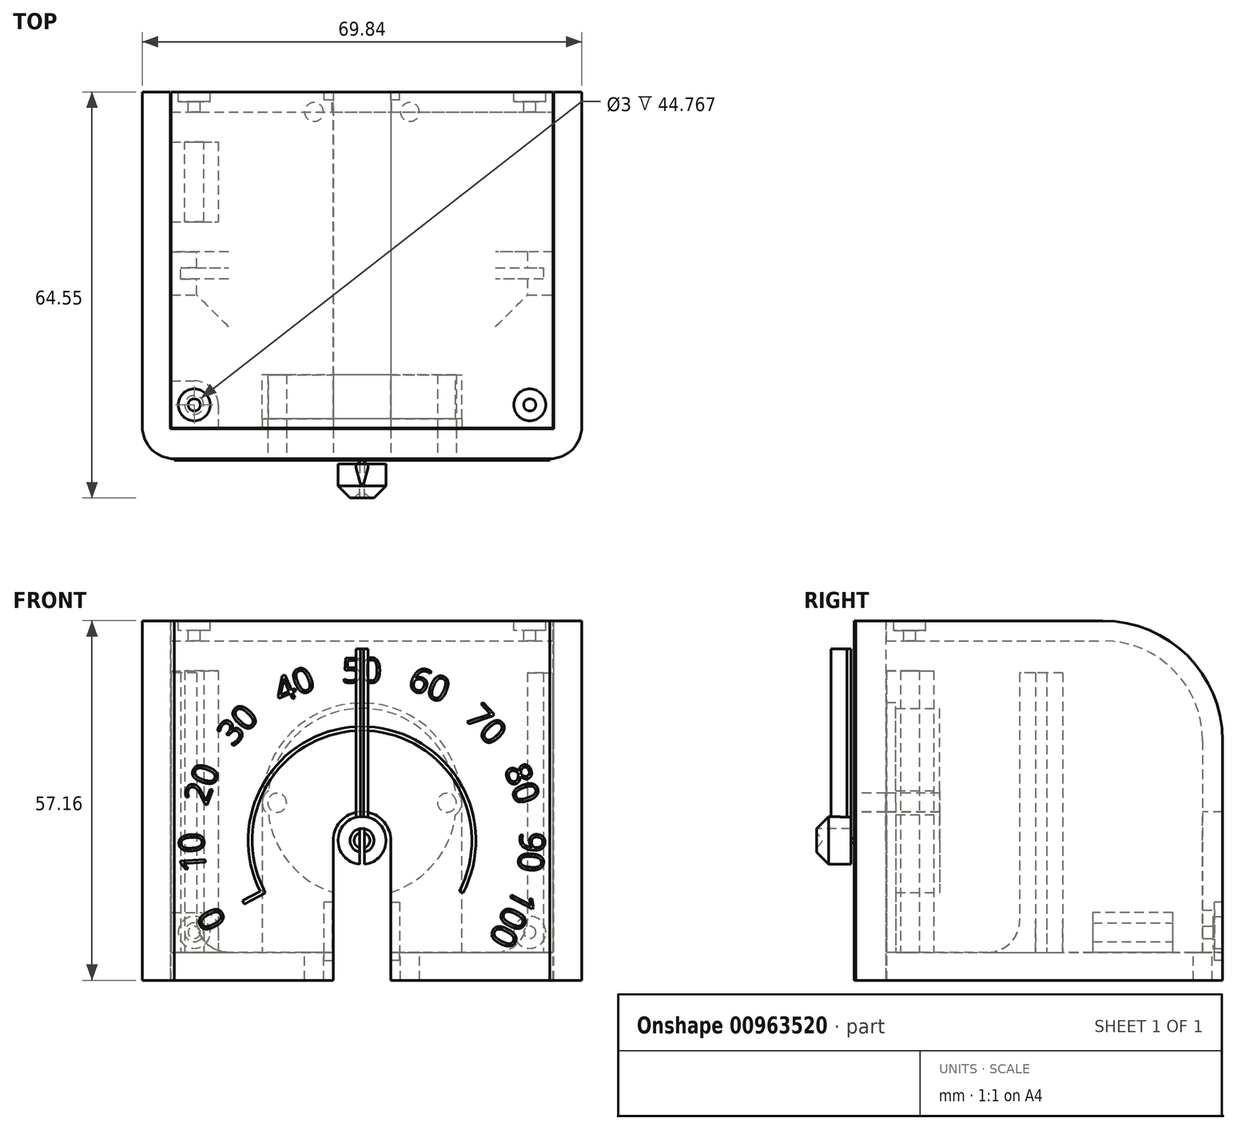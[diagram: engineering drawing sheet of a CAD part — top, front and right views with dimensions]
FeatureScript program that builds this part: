
annotation { "Feature Type Name" : "Feature", "Feature Type Description" : "" }
export const myFeature = defineFeature(function(context is Context, id is Id, definition is map)
    precondition{}
    {
        {
            var Q0;
            Q0=qCreatedBy(makeId("Front.planeOp"),FACE);
            var sketch = newSketch(context, id + "F0", { "sketchPlane" : qUnion([Q0])});
            skArc(sketch, "E0", {"start": v(-14.88, -1.9) * mm, "mid": v(0, -15) * mm, "end": v(14.88, -1.9) * mm});
            skArc(sketch, "E1", {"start": v(-14.88, 1.9) * mm, "mid": v(-15.85, 0) * mm, "end": v(-14.88, -1.9) * mm});
            skArc(sketch, "E2", {"start": v(14.88, -1.9) * mm, "mid": v(15.85, 0) * mm, "end": v(14.88, 1.9) * mm});
            skLineSegment(sketch, "E3", {"start": v(13.5, 0) * mm, "end": v(-13.5, 0) * mm, "construction": true});
            skArc(sketch, "E4.trimOffspring", {"start": v(14.88, 1.9) * mm, "mid": v(0, 15) * mm, "end": v(-14.88, 1.9) * mm});
            skCircle(sketch, "E5", {"center": v(-13.5, 0) * mm, "radius": 0.93 * mm});
            skCircle(sketch, "E6", {"center": v(13.5, 0) * mm, "radius": 0.93 * mm});
            skSolve(sketch);
        }
        {
            var Q0;
            Q0=qSketchRegion(id+"F0",true);
            extrude(context, id + "F1", {"entities" : qUnion([Q0]), "depth" : 7 * mm, "offsetDistance" : 25.4 * mm});
        }
        {
            var Q0;
            Q0=qCreatedBy(makeId("Right.planeOp"),FACE);
            var sketch = newSketch(context, id + "F2", { "sketchPlane" : qUnion([Q0])});
            skLineSegment(sketch, "E7.0", {"start": v(-7, -1.9) * mm, "end": v(-7, -15) * mm, "construction": true});
            skLineSegment(sketch, "E8", {"start": v(-7, -6) * mm, "end": v(-18, -6) * mm});
            skLineSegment(sketch, "E9", {"start": v(-18, -6) * mm, "end": v(-18, -5.5) * mm});
            skLineSegment(sketch, "E10", {"start": v(-18, -5.5) * mm, "end": v(-9.5, -5.5) * mm});
            skLineSegment(sketch, "E11", {"start": v(-9.5, -5.5) * mm, "end": v(-9.5, -5) * mm});
            skLineSegment(sketch, "E12", {"start": v(-9.5, -5) * mm, "end": v(-7, -5) * mm});
            skLineSegment(sketch, "E13", {"start": v(-7, -5) * mm, "end": v(-7, -6) * mm});
            skSolve(sketch);
        }
        {
            var Q0;
            Q0=qSketchRegion(id+"F2",true);
            var Q1;
            Q1=sQuery(id+"F2.wireOp",EDGE,"E8");
            revolve(context, id + "F3", {"operationType" : NewBodyOperationType.ADD, "surfaceOperationType" : NewSurfaceOperationType.NEW, "entities" : qUnion([Q0]), "axis" : qUnion([Q1]), "revolveType" : RevolveType.FULL});
        }
        {
            var Q0;
            Q0=makeQuery(id+"F3.opRevolve","SWEPT_EDGE",EDGE,{"disambiguationData":[OSD([sQuery(id+"F2.wireOp",EDGE,"E9"),sQuery(id+"F2.wireOp",EDGE,"E10")])]});
            chamfer(context, id + "F4", {"entities" : qUnion([Q0]), "chamferType" : ChamferType.OFFSET_ANGLE, "width" : 0.25 * mm, "oppositeDirection" : false, "angle" : 30 * degree, "tangentPropagation" : true});
        }
        {
            var Q0;
            Q0=makeQuery(id+"F1.opExtrude","CAP_FACE",FACE,{"disambiguationData":[OSD([sQuery(id+"F0.wireOp",EDGE,"E0"),sQuery(id+"F0.wireOp",EDGE,"E1"),sQuery(id+"F0.wireOp",EDGE,"E2"),sQuery(id+"F0.wireOp",EDGE,"E4.trimOffspring"),sQuery(id+"F0.wireOp",EDGE,"E5"),sQuery(id+"F0.wireOp",EDGE,"E6")])],"isStart":false});
            cPlane(context, id + "F5", {"entities" : qUnion([Q0]), "cplaneType" : CPlaneType.OFFSET, "offset" : 1.59 * mm, "width" : 152.4 * mm, "height" : 152.4 * mm});
        }
        {
            var Q0;
            Q0=qCreatedBy(id+"F5.planeOp",FACE);
            var sketch = newSketch(context, id + "F6", { "sketchPlane" : qUnion([Q0])});
            skLineSegment(sketch, "E14.bottom", {"start": v(-34.93, -25.05) * mm, "end": v(34.93, -25.05) * mm});
            skLineSegment(sketch, "E14.top", {"start": v(-34.93, 28.93) * mm, "end": v(34.93, 28.93) * mm});
            skLineSegment(sketch, "E14.left", {"start": v(-34.92, -25.05) * mm, "end": v(-34.92, 28.93) * mm});
            skLineSegment(sketch, "E14.right", {"start": v(34.92, -25.05) * mm, "end": v(34.92, 28.93) * mm});
            skPoint(sketch, "E14.middle", {"position": v(0, 0) * mm});
            skCircle(sketch, "E15.0", {"center": v(0, -6) * mm, "radius": 2.27 * mm});
            skLineSegment(sketch, "E16", {"start": v(0, 28.93) * mm, "end": v(0, 0) * mm, "construction": true});
            skLineSegment(sketch, "E17", {"start": v(0, -6) * mm, "end": v(22.45, 16.45) * mm, "construction": true});
            skLineSegment(sketch, "E18", {"start": v(0, -6) * mm, "end": v(-22.45, 16.45) * mm, "construction": true});
            skLineSegment(sketch, "E19", {"start": v(0, -6) * mm, "end": v(-27.5, -21.87) * mm, "construction": true});
            skLineSegment(sketch, "E20", {"start": v(0, -6) * mm, "end": v(27.5, -21.87) * mm, "construction": true});
            skLineSegment(sketch, "E21", {"start": v(0, -6) * mm, "end": v(0, 25.75) * mm, "construction": true});
            skCircle(sketch, "E22", {"center": v(0, -6) * mm, "radius": 31.75 * mm, "construction": true});
            skSolve(sketch);
        }
        {
            var Q0;
            Q0=qSketchRegion(id+"F6",true);
            extrude(context, id + "F7", {"entities" : qUnion([Q0]), "depth" : 4.76 * mm, "offsetDistance" : 25.4 * mm});
        }
        {
            var Q0;
            Q0=makeQuery(id+"F7.opExtrude","SWEPT_FACE",FACE,{"disambiguationData":[OSD([sQuery(id+"F6.wireOp",EDGE,"E14.bottom")])]});
            var sketch = newSketch(context, id + "F8", { "sketchPlane" : qUnion([Q0])});
            skLineSegment(sketch, "E23", {"start": v(-28.83, -15.24) * mm, "end": v(-26.29, -15.24) * mm});
            skLineSegment(sketch, "E24", {"start": v(-26.29, -15.24) * mm, "end": v(-26.29, -12.7) * mm});
            skLineSegment(sketch, "E25", {"start": v(-26.29, -12.7) * mm, "end": v(-31.75, -12.7) * mm});
            skLineSegment(sketch, "E26", {"start": v(-31.75, -12.7) * mm, "end": v(-31.75, -19.56) * mm});
            skLineSegment(sketch, "E27", {"start": v(-31.75, -19.56) * mm, "end": v(-26.29, -19.56) * mm});
            skLineSegment(sketch, "E28", {"start": v(-26.29, -19.56) * mm, "end": v(-26.29, -17.02) * mm});
            skLineSegment(sketch, "E29", {"start": v(-26.29, -17.02) * mm, "end": v(-28.83, -17.02) * mm});
            skLineSegment(sketch, "E30", {"start": v(-28.83, -17.02) * mm, "end": v(-28.83, -15.24) * mm});
            skLineSegment(sketch, "E31", {"start": v(-28.83, -16.13) * mm, "end": v(-31.75, -16.13) * mm, "construction": true});
            skSolve(sketch);
        }
        {
            var Q0;
            Q0 = qSketchRegion(id + "F8", true);
            extrude(context, id + "F9", {"entities" : qUnion([Q0]), "oppositeDirection" : true, "depth" : 45.72 * mm, "offsetDistance" : 25.4 * mm});
        }
        {
            var Q0;
            Q0=makeQuery(id+"F9.opExtrude","SWEPT_BODY",BODY,{"disambiguationData":[OSD([sQuery(id+"F8.wireOp",EDGE,"E23"),sQuery(id+"F8.wireOp",EDGE,"E24"),sQuery(id+"F8.wireOp",EDGE,"E25"),sQuery(id+"F8.wireOp",EDGE,"E26"),sQuery(id+"F8.wireOp",EDGE,"E27"),sQuery(id+"F8.wireOp",EDGE,"E28"),sQuery(id+"F8.wireOp",EDGE,"E29"),sQuery(id+"F8.wireOp",EDGE,"E30")])]});
            var Q1;
            Q1=qCreatedBy(makeId("Right.planeOp"),FACE);
            mirror(context, id + "F10", {"entities" : qUnion([Q0]), "mirrorPlane" : qUnion([Q1])});
        }
        {
            var Q0;
            Q0=makeQuery(id+"F7.opExtrude","CAP_FACE",FACE,{"disambiguationData":[OSD([sQuery(id+"F6.wireOp",EDGE,"E14.bottom"),sQuery(id+"F6.wireOp",EDGE,"E14.top"),sQuery(id+"F6.wireOp",EDGE,"E14.left"),sQuery(id+"F6.wireOp",EDGE,"E14.right"),sQuery(id+"F6.wireOp",EDGE,"E15.0")])],"isStart":true});
            var sketch = newSketch(context, id + "F11", { "sketchPlane" : qUnion([Q0])});
            skLineSegment(sketch, "E32", {"start": v(-34.92, 28.93) * mm, "end": v(-34.92, -28.23) * mm});
            skLineSegment(sketch, "E33", {"start": v(-34.92, -28.23) * mm, "end": v(34.93, -28.23) * mm});
            skLineSegment(sketch, "E34", {"start": v(34.92, -28.23) * mm, "end": v(34.92, 28.93) * mm});
            skLineSegment(sketch, "E35", {"start": v(34.93, 28.93) * mm, "end": v(31.75, 28.93) * mm});
            skLineSegment(sketch, "E36", {"start": v(31.75, 28.93) * mm, "end": v(31.75, -25.05) * mm, "construction": true});
            skLineSegment(sketch, "E37", {"start": v(31.75, -25.05) * mm, "end": v(-31.75, -25.05) * mm, "construction": true});
            skLineSegment(sketch, "E38", {"start": v(-31.75, -25.05) * mm, "end": v(-31.75, 28.93) * mm, "construction": true});
            skLineSegment(sketch, "E39", {"start": v(-31.75, 28.93) * mm, "end": v(-34.92, 28.93) * mm});
            skLineSegment(sketch, "E40.0", {"start": v(-30.48, -23.78) * mm, "end": v(-30.48, 28.93) * mm});
            skLineSegment(sketch, "E40.1", {"start": v(30.48, -23.78) * mm, "end": v(-30.48, -23.78) * mm});
            skLineSegment(sketch, "E40.2", {"start": v(30.48, 28.93) * mm, "end": v(30.48, -23.78) * mm});
            skLineSegment(sketch, "E41", {"start": v(-30.48, 28.93) * mm, "end": v(-31.75, 28.93) * mm});
            skLineSegment(sketch, "E42", {"start": v(30.48, 28.93) * mm, "end": v(31.75, 28.93) * mm});
            skSolve(sketch);
        }
        {
            var Q0;
            Q0 = qSketchRegion(id + "F11", true);
            var Q1;
            Q1=makeQuery(id+"F9.opExtrude","SWEPT_FACE",FACE,{"disambiguationData":[OSD([sQuery(id+"F8.wireOp",EDGE,"E27")])]});
            var Q2;
            Q2=makeQuery(id+"F7.opExtrude","CAP_FACE",FACE,{"disambiguationData":[OSD([sQuery(id+"F6.wireOp",EDGE,"E14.bottom"),sQuery(id+"F6.wireOp",EDGE,"E14.top"),sQuery(id+"F6.wireOp",EDGE,"E14.left"),sQuery(id+"F6.wireOp",EDGE,"E14.right"),sQuery(id+"F6.wireOp",EDGE,"E15.0")])],"isStart":false});
            extrude(context, id + "F12", {"entities" : qUnion([Q0]), "operationType" : NewBodyOperationType.ADD, "endBound" : BoundingType.UP_TO_SURFACE, "depth" : 25.4 * mm, "endBoundEntityFace" : qUnion([Q1]), "hasOffset" : true, "offsetDistance" : 25.4 * mm, "offsetOppositeDirection" : true, "hasSecondDirection" : true, "secondDirectionBound" : SecondDirectionBoundingType.UP_TO_SURFACE, "secondDirectionOppositeDirection" : true, "secondDirectionDepth" : 25.4 * mm, "secondDirectionBoundEntityFace" : qUnion([Q2])});
        }
        {
            var Q0;
            Q0=makeQuery(id+"F7.opExtrude","CAP_FACE",FACE,{"disambiguationData":[OSD([sQuery(id+"F6.wireOp",EDGE,"E14.bottom"),sQuery(id+"F6.wireOp",EDGE,"E14.top"),sQuery(id+"F6.wireOp",EDGE,"E14.left"),sQuery(id+"F6.wireOp",EDGE,"E14.right"),sQuery(id+"F6.wireOp",EDGE,"E15.0")])],"isStart":true});
            var sketch = newSketch(context, id + "F13", { "sketchPlane" : qUnion([Q0])});
            skArc(sketch, "E43", {"start": v(15.85, 0) * mm, "mid": v(0, 15.85) * mm, "end": v(-15.85, 0) * mm});
            skLineSegment(sketch, "E44", {"start": v(-15.85, 0) * mm, "end": v(-15.85, -23.78) * mm});
            skLineSegment(sketch, "E45", {"start": v(-15.85, -23.78) * mm, "end": v(15.85, -23.78) * mm});
            skLineSegment(sketch, "E46", {"start": v(15.85, -23.78) * mm, "end": v(15.85, 0) * mm});
            skCircle(sketch, "E47.0", {"center": v(0, -6) * mm, "radius": 2.27 * mm});
            skSolve(sketch);
        }
        {
            var Q0;
            Q0 = qSketchRegion(id + "F13", true);
            var Q1;
            Q1=makeQuery(id+"F1.opExtrude","CAP_FACE",FACE,{"disambiguationData":[OSD([sQuery(id+"F0.wireOp",EDGE,"E0"),sQuery(id+"F0.wireOp",EDGE,"E1"),sQuery(id+"F0.wireOp",EDGE,"E2"),sQuery(id+"F0.wireOp",EDGE,"E4.trimOffspring"),sQuery(id+"F0.wireOp",EDGE,"E5"),sQuery(id+"F0.wireOp",EDGE,"E6")])],"isStart":false});
            extrude(context, id + "F14", {"entities" : qUnion([Q0]), "operationType" : NewBodyOperationType.ADD, "endBound" : BoundingType.UP_TO_SURFACE, "depth" : 25.4 * mm, "endBoundEntityFace" : qUnion([Q1]), "offsetDistance" : 25.4 * mm});
        }
        {
            var Q0;
            Q0=makeQuery(id+"F12.boolean.opBoolean","MERGE",FACE,{"derivedFrom":[makeQuery(id+"F7.opExtrude","CAP_FACE",FACE,{"disambiguationData":[OSD([sQuery(id+"F6.wireOp",EDGE,"E14.bottom"),sQuery(id+"F6.wireOp",EDGE,"E14.top"),sQuery(id+"F6.wireOp",EDGE,"E14.left"),sQuery(id+"F6.wireOp",EDGE,"E14.right"),sQuery(id+"F6.wireOp",EDGE,"E15.0")])],"isStart":false}),makeQuery(id+"F12.opExtrude","CAP_FACE",FACE,{"disambiguationData":[OSD([sQuery(id+"F11.wireOp",EDGE,"E32"),sQuery(id+"F11.wireOp",EDGE,"E33"),sQuery(id+"F11.wireOp",EDGE,"E34"),sQuery(id+"F11.wireOp",EDGE,"E35"),sQuery(id+"F11.wireOp",EDGE,"E39"),sQuery(id+"F11.wireOp",EDGE,"E40.0"),sQuery(id+"F11.wireOp",EDGE,"E40.1"),sQuery(id+"F11.wireOp",EDGE,"E40.2"),sQuery(id+"F11.wireOp",EDGE,"E41"),sQuery(id+"F11.wireOp",EDGE,"E42")])],"isStart":true})]});
            var sketch = newSketch(context, id + "F15", { "sketchPlane" : qUnion([Q0])});
            skCircle(sketch, "E48.0", {"center": v(13.5, 0) * mm, "radius": 0.93 * mm, "construction": true});
            skCircle(sketch, "E48.1", {"center": v(-13.5, 0) * mm, "radius": 0.93 * mm, "construction": true});
            skCircle(sketch, "E49", {"center": v(-13.5, 0) * mm, "radius": 1.5 * mm});
            skCircle(sketch, "E50", {"center": v(13.5, 0) * mm, "radius": 1.5 * mm});
            skSolve(sketch);
        }
        {
            var Q0;
            Q0 = qSketchRegion(id + "F15", true);
            extrude(context, id + "F16", {"entities" : qUnion([Q0]), "operationType" : NewBodyOperationType.REMOVE, "endBound" : BoundingType.UP_TO_NEXT, "oppositeDirection" : true, "depth" : 25.4 * mm, "offsetDistance" : 25.4 * mm});
        }
        {
            var Q0;
            Q0=makeQuery(id+"F12.boolean.opBoolean","INTERSECT",EDGE,{"derivedFrom":[makeQuery(id+"F10.opPattern","COPY",FACE,{"derivedFrom":makeQuery(id+"F9.opExtrude","SWEPT_FACE",FACE,{"disambiguationData":[OSD([sQuery(id+"F8.wireOp",EDGE,"E25")])]}),"instanceName":"1"}),makeQuery(id+"F12.opExtrude","SWEPT_FACE",FACE,{"disambiguationData":[OSD([sQuery(id+"F11.wireOp",EDGE,"E40.1")])]})]});
            var Q1;
            Q1=makeQuery(id+"F12.boolean.opBoolean","INTERSECT",EDGE,{"derivedFrom":[makeQuery(id+"F9.opExtrude","SWEPT_FACE",FACE,{"disambiguationData":[OSD([sQuery(id+"F8.wireOp",EDGE,"E25")])]}),makeQuery(id+"F12.opExtrude","SWEPT_FACE",FACE,{"disambiguationData":[OSD([sQuery(id+"F11.wireOp",EDGE,"E40.1")])]})]});
            var Q2;
            Q2=makeQuery(id+"F12.boolean.opBoolean","INTERSECT",EDGE,{"derivedFrom":[makeQuery(id+"F9.opExtrude","SWEPT_FACE",FACE,{"disambiguationData":[OSD([sQuery(id+"F8.wireOp",EDGE,"E24")])]}),makeQuery(id+"F12.opExtrude","SWEPT_FACE",FACE,{"disambiguationData":[OSD([sQuery(id+"F11.wireOp",EDGE,"E40.1")])]})]});
            var Q3;
            Q3=makeQuery(id+"F12.boolean.opBoolean","INTERSECT",EDGE,{"derivedFrom":[makeQuery(id+"F9.opExtrude","SWEPT_FACE",FACE,{"disambiguationData":[OSD([sQuery(id+"F8.wireOp",EDGE,"E28")])]}),makeQuery(id+"F12.opExtrude","SWEPT_FACE",FACE,{"disambiguationData":[OSD([sQuery(id+"F11.wireOp",EDGE,"E40.1")])]})]});
            var Q4;
            Q4=makeQuery(id+"F12.boolean.opBoolean","INTERSECT",EDGE,{"derivedFrom":[makeQuery(id+"F10.opPattern","COPY",FACE,{"derivedFrom":makeQuery(id+"F9.opExtrude","SWEPT_FACE",FACE,{"disambiguationData":[OSD([sQuery(id+"F8.wireOp",EDGE,"E24")])]}),"instanceName":"1"}),makeQuery(id+"F12.opExtrude","SWEPT_FACE",FACE,{"disambiguationData":[OSD([sQuery(id+"F11.wireOp",EDGE,"E40.1")])]})]});
            var Q5;
            Q5=makeQuery(id+"F12.boolean.opBoolean","INTERSECT",EDGE,{"derivedFrom":[makeQuery(id+"F10.opPattern","COPY",FACE,{"derivedFrom":makeQuery(id+"F9.opExtrude","SWEPT_FACE",FACE,{"disambiguationData":[OSD([sQuery(id+"F8.wireOp",EDGE,"E28")])]}),"instanceName":"1"}),makeQuery(id+"F12.opExtrude","SWEPT_FACE",FACE,{"disambiguationData":[OSD([sQuery(id+"F11.wireOp",EDGE,"E40.1")])]})]});
            fillet(context, id + "F17", {"entities" : qUnion([Q0, Q1, Q2, Q3, Q4, Q5]), "radius" : 5.08 * mm, "tangentPropagation" : true, "allowEdgeOverflow" : false});
        }
        {
            var Q0;
            Q0=makeQuery(id+"F12.opExtrude","SWEPT_FACE",FACE,{"disambiguationData":[OSD([sQuery(id+"F11.wireOp",EDGE,"E40.1")])]});
            var sketch = newSketch(context, id + "F18", { "sketchPlane" : qUnion([Q0])});
            skLineSegment(sketch, "E51.bottom", {"start": v(-30.48, -0.97) * mm, "end": v(-26.67, -0.97) * mm});
            skLineSegment(sketch, "E51.right", {"start": v(-22.86, -4.78) * mm, "end": v(-22.86, -8.59) * mm});
            skPoint(sketch, "E52.visualSharp", {"position": v(-22.86, -0.97) * mm});
            skArc(sketch, "E52.filletArc", {"start": v(-22.86, -4.78) * mm, "mid": v(-23.98, -2.08) * mm, "end": v(-26.67, -0.97) * mm});
            skCircle(sketch, "E53", {"center": v(-26.67, -4.78) * mm, "radius": 1.5 * mm});
            skLineSegment(sketch, "E54", {"start": v(-30.48, -8.59) * mm, "end": v(-30.48, -0.97) * mm});
            skLineSegment(sketch, "E55", {"start": v(-30.48, -8.59) * mm, "end": v(-22.86, -8.59) * mm});
            skSolve(sketch);
        }
        {
            var Q0;
            Q0 = qSketchRegion(id + "F18", true);
            var Q1;
            Q1=makeQuery(id+"F12.boolean.opBoolean","MERGE",FACE,{"derivedFrom":[makeQuery(id+"F7.opExtrude","SWEPT_FACE",FACE,{"disambiguationData":[OSD([sQuery(id+"F6.wireOp",EDGE,"E14.top")])]}),makeQuery(id+"F12.opExtrude","SWEPT_FACE",FACE,{"disambiguationData":[OSD([sQuery(id+"F11.wireOp",EDGE,"E35"),sQuery(id+"F11.wireOp",EDGE,"E42")])]}),makeQuery(id+"F12.opExtrude","SWEPT_FACE",FACE,{"disambiguationData":[OSD([sQuery(id+"F11.wireOp",EDGE,"E39"),sQuery(id+"F11.wireOp",EDGE,"E41")])]})]});
            extrude(context, id + "F19", {"entities" : qUnion([Q0]), "operationType" : NewBodyOperationType.ADD, "endBound" : BoundingType.UP_TO_SURFACE, "depth" : 25.4 * mm, "endBoundEntityFace" : qUnion([Q1]), "hasOffset" : true, "offsetDistance" : 7.94 * mm});
        }
        {
            var Q0;
            Q0=makeQuery(id+"F12.opExtrude","CAP_EDGE",EDGE,{"disambiguationData":[OSD([sQuery(id+"F11.wireOp",EDGE,"E35"),sQuery(id+"F11.wireOp",EDGE,"E42")])],"isStart":false});
            var Q1;
            Q1=makeQuery(id+"F12.opExtrude","CAP_EDGE",EDGE,{"disambiguationData":[OSD([sQuery(id+"F11.wireOp",EDGE,"E39"),sQuery(id+"F11.wireOp",EDGE,"E41")])],"isStart":false});
            fillet(context, id + "F20", {"entities" : qUnion([Q0, Q1]), "radius" : 19.05 * mm, "tangentPropagation" : true, "allowEdgeOverflow" : false});
        }
        {
            var Q0;
            Q0=makeQuery(id+"F12.boolean.opBoolean","MERGE",EDGE,{"derivedFrom":[makeQuery(id+"F7.opExtrude","CAP_EDGE",EDGE,{"disambiguationData":[OSD([sQuery(id+"F6.wireOp",EDGE,"E14.right")])],"isStart":false}),makeQuery(id+"F12.opExtrude","CAP_EDGE",EDGE,{"disambiguationData":[OSD([sQuery(id+"F11.wireOp",EDGE,"E32")])],"isStart":true})]});
            var Q1;
            Q1=makeQuery(id+"F12.boolean.opBoolean","MERGE",EDGE,{"derivedFrom":[makeQuery(id+"F7.opExtrude","CAP_EDGE",EDGE,{"disambiguationData":[OSD([sQuery(id+"F6.wireOp",EDGE,"E14.left")])],"isStart":false}),makeQuery(id+"F12.opExtrude","CAP_EDGE",EDGE,{"disambiguationData":[OSD([sQuery(id+"F11.wireOp",EDGE,"E34")])],"isStart":true})]});
            fillet(context, id + "F21", {"entities" : qUnion([Q0, Q1]), "radius" : 5.08 * mm, "tangentPropagation" : true, "allowEdgeOverflow" : false});
        }
        {
            var Q0;
            {var subQ0=sQuery(id+"F11.wireOp",EDGE,"E40.1");var subQ1=makeQuery(id+"F12.opExtrude","SWEPT_FACE",FACE,{"disambiguationData":[OSD([subQ0])]});var subQ11=makeQuery(id+"F9.opExtrude","SWEPT_FACE",FACE,{"disambiguationData":[OSD([sQuery(id+"F8.wireOp",EDGE,"E23")])]});Q0=makeQuery(id+"FiTiTFmtsTyTFf0_2.1.F19.boolean.opBoolean","SPLIT",FACE,{"disambiguationData":[TD([subQ11])],"derivedFrom":makeQuery(id+"F19.boolean.opBoolean","SPLIT",FACE,{"disambiguationData":[TD([subQ11])],"derivedFrom":subQ1})});}
            var sketch = newSketch(context, id + "F22", { "sketchPlane" : qUnion([Q0])});
            skLineSegment(sketch, "E56.bottom", {"start": v(-30.48, 37.02) * mm, "end": v(-22.86, 37.02) * mm});
            skLineSegment(sketch, "E56.top", {"start": v(-30.48, 24.32) * mm, "end": v(-22.86, 24.32) * mm});
            skLineSegment(sketch, "E56.left", {"start": v(-30.48, 37.02) * mm, "end": v(-30.48, 24.32) * mm});
            skLineSegment(sketch, "E56.right", {"start": v(-22.86, 37.02) * mm, "end": v(-22.86, 24.32) * mm});
            skSolve(sketch);
        }
        {
            var Q0;
            Q0 = qSketchRegion(id + "F22", true);
            extrude(context, id + "F23", {"entities" : qUnion([Q0]), "operationType" : NewBodyOperationType.ADD, "depth" : 6.35 * mm, "offsetDistance" : 25.4 * mm});
        }
        {
            var Q0;
            Q0=makeQuery(id+"F23.opExtrude","CAP_EDGE",EDGE,{"disambiguationData":[OSD([sQuery(id+"F22.wireOp",EDGE,"E56.right")])],"isStart":false});
            fillet(context, id + "F24", {"entities" : qUnion([Q0]), "radius" : 2.54 * mm, "tangentPropagation" : true, "allowEdgeOverflow" : false});
        }
        {
            var Q0;
            Q0=makeQuery(id+"F23.opExtrude","SWEPT_FACE",FACE,{"disambiguationData":[OSD([sQuery(id+"F22.wireOp",EDGE,"E56.bottom")])]});
            var sketch = newSketch(context, id + "F25", { "sketchPlane" : qUnion([Q0])});
            skLineSegment(sketch, "E57", {"start": v(22.86, -23.78) * mm, "end": v(30.48, -17.43) * mm, "construction": true});
            skCircle(sketch, "E58", {"center": v(26.67, -20.6) * mm, "radius": 1.5 * mm});
            skSolve(sketch);
        }
        {
            var Q0;
            Q0 = qSketchRegion(id + "F25", true);
            extrude(context, id + "F26", {"entities" : qUnion([Q0]), "operationType" : NewBodyOperationType.REMOVE, "endBound" : BoundingType.UP_TO_NEXT, "oppositeDirection" : true, "depth" : 25.4 * mm, "offsetDistance" : 25.4 * mm});
        }
        {
            var Q0;
            Q0=makeQuery(id+"F12.opExtrude","SWEPT_FACE",FACE,{"disambiguationData":[OSD([sQuery(id+"F11.wireOp",EDGE,"E40.0")])]});
            var sketch = newSketch(context, id + "F27", { "sketchPlane" : qUnion([Q0])});
            skLineSegment(sketch, "E59.0", {"start": v(-25.9, 28.93) * mm, "end": v(8.59, 28.93) * mm});
            skArc(sketch, "E59.1", {"start": v(-25.9, 28.93) * mm, "mid": v(-39.38, 23.35) * mm, "end": v(-44.96, 9.88) * mm});
            skLineSegment(sketch, "E59.2", {"start": v(-44.96, -23.78) * mm, "end": v(-44.96, 9.88) * mm});
            skLineSegment(sketch, "E60.0", {"start": v(-25.9, 25.75) * mm, "end": v(8.59, 25.75) * mm});
            skArc(sketch, "E60.1", {"start": v(-25.9, 25.75) * mm, "mid": v(-37.13, 21.1) * mm, "end": v(-41.78, 9.88) * mm});
            skLineSegment(sketch, "E60.2", {"start": v(-41.78, -23.78) * mm, "end": v(-41.78, 9.88) * mm});
            skLineSegment(sketch, "E61", {"start": v(-41.78, -23.78) * mm, "end": v(-44.96, -23.78) * mm});
            skLineSegment(sketch, "E62", {"start": v(8.59, 28.93) * mm, "end": v(8.59, 25.75) * mm});
            skSolve(sketch);
        }
        {
            var Q0;
            Q0 = qSketchRegion(id + "F27", true);
            var Q1;
            Q1=makeQuery(id+"F12.opExtrude","SWEPT_FACE",FACE,{"disambiguationData":[OSD([sQuery(id+"F11.wireOp",EDGE,"E40.2")])]});
            extrude(context, id + "F28", {"entities" : qUnion([Q0]), "endBound" : BoundingType.UP_TO_SURFACE, "depth" : 25.4 * mm, "endBoundEntityFace" : qUnion([Q1]), "offsetDistance" : 25.4 * mm});
        }
        {
            var Q0;
            Q0=makeQuery(id+"F28.opExtrude","SWEPT_FACE",FACE,{"disambiguationData":[OSD([sQuery(id+"F27.wireOp",EDGE,"E59.0")])]});
            var sketch = newSketch(context, id + "F29", { "sketchPlane" : qUnion([Q0])});
            skCircle(sketch, "E63.0", {"center": v(-26.67, -4.78) * mm, "radius": 1.5 * mm});
            skCircle(sketch, "E63.1", {"center": v(26.67, -4.78) * mm, "radius": 1.5 * mm});
            skSolve(sketch);
        }
        {
            var Q0;
            Q0=sQuery(id+"F29.wireOp",VERTEX,"E63.0.center");
            var Q1;
            Q1=sQuery(id+"F29.wireOp",VERTEX,"E63.1.center");
            var Q2;
            Q2=makeQuery(id+"F7.opExtrude","SWEPT_BODY",BODY,{"disambiguationData":[OSD([sQuery(id+"F6.wireOp",EDGE,"E14.bottom"),sQuery(id+"F6.wireOp",EDGE,"E14.top"),sQuery(id+"F6.wireOp",EDGE,"E14.left"),sQuery(id+"F6.wireOp",EDGE,"E14.right"),sQuery(id+"F6.wireOp",EDGE,"E15.0")])]});
            var Q3;
            Q3=makeQuery(id+"F28.opExtrude","SWEPT_BODY",BODY,{"disambiguationData":[OSD([sQuery(id+"F27.wireOp",EDGE,"E59.0"),sQuery(id+"F27.wireOp",EDGE,"E59.1"),sQuery(id+"F27.wireOp",EDGE,"E59.2"),sQuery(id+"F27.wireOp",EDGE,"E60.0"),sQuery(id+"F27.wireOp",EDGE,"E60.1"),sQuery(id+"F27.wireOp",EDGE,"E60.2"),sQuery(id+"F27.wireOp",EDGE,"E61"),sQuery(id+"F27.wireOp",EDGE,"E62")])]});
            hole(context, id + "F30", {"style" : HoleStyle.C_BORE, "endStyle" : HoleEndStyle.THROUGH, "holeDiameter" : 1.93 * mm, "cBoreDiameter" : 5.08 * mm, "cBoreDepth" : 1.52 * mm, "majorDiameter" : 6.35 * mm, "isTappedThrough" : true, "tappedDepth" : 12.7 * mm, "tapClearance" : 3, "locations" : qUnion([Q0, Q1]), "scope" : qUnion([Q2, Q3])});
        }
        {
            var Q0;
            Q0=makeQuery(id+"F28.opExtrude","SWEPT_FACE",FACE,{"disambiguationData":[OSD([sQuery(id+"F27.wireOp",EDGE,"E59.2")])]});
            var sketch = newSketch(context, id + "F31", { "sketchPlane" : qUnion([Q0])});
            skCircle(sketch, "E64.0", {"center": v(-26.67, -20.6) * mm, "radius": 1.5 * mm});
            skCircle(sketch, "E65.0", {"center": v(26.67, -20.6) * mm, "radius": 1.5 * mm});
            skSolve(sketch);
        }
        {
            var Q0;
            Q0=sQuery(id+"F31.wireOp",VERTEX,"E65.0.center");
            var Q1;
            Q1=sQuery(id+"F31.wireOp",VERTEX,"E64.0.center");
            var Q2;
            Q2=makeQuery(id+"F28.opExtrude","SWEPT_BODY",BODY,{"disambiguationData":[OSD([sQuery(id+"F27.wireOp",EDGE,"E59.0"),sQuery(id+"F27.wireOp",EDGE,"E59.1"),sQuery(id+"F27.wireOp",EDGE,"E59.2"),sQuery(id+"F27.wireOp",EDGE,"E60.0"),sQuery(id+"F27.wireOp",EDGE,"E60.1"),sQuery(id+"F27.wireOp",EDGE,"E60.2"),sQuery(id+"F27.wireOp",EDGE,"E61"),sQuery(id+"F27.wireOp",EDGE,"E62")])]});
            hole(context, id + "F32", {"style" : HoleStyle.C_BORE, "endStyle" : HoleEndStyle.THROUGH, "holeDiameter" : 1.93 * mm, "cBoreDiameter" : 5.08 * mm, "cBoreDepth" : 1.52 * mm, "majorDiameter" : 6.35 * mm, "isTappedThrough" : true, "tappedDepth" : 12.7 * mm, "tapClearance" : 3, "locations" : qUnion([Q0, Q1]), "scope" : qUnion([Q2])});
        }
        {
            var Q0;
            {var subQ0=sQuery(id+"F11.wireOp",EDGE,"E40.1");var subQ1=makeQuery(id+"F12.opExtrude","SWEPT_FACE",FACE,{"disambiguationData":[OSD([subQ0])]});var subQ11=makeQuery(id+"F9.opExtrude","SWEPT_FACE",FACE,{"disambiguationData":[OSD([sQuery(id+"F8.wireOp",EDGE,"E23")])]});Q0=makeQuery(id+"FiTiTFmtsTyTFf0_2.1.F19.boolean.opBoolean","SPLIT",FACE,{"disambiguationData":[TD([subQ11])],"derivedFrom":makeQuery(id+"F19.boolean.opBoolean","SPLIT",FACE,{"disambiguationData":[TD([subQ11])],"derivedFrom":subQ1})});}
            var sketch = newSketch(context, id + "F33", { "sketchPlane" : qUnion([Q0])});
            skLineSegment(sketch, "E66", {"start": v(-7.62, 41.78) * mm, "end": v(7.62, 41.78) * mm, "construction": true});
            skPoint(sketch, "E67", {"position": v(0, 41.78) * mm});
            skCircle(sketch, "E68", {"center": v(-7.62, 41.78) * mm, "radius": 1.5 * mm});
            skCircle(sketch, "E69", {"center": v(7.62, 41.78) * mm, "radius": 1.5 * mm});
            skSolve(sketch);
        }
        {
            var Q0;
            Q0 = qSketchRegion(id + "F33", true);
            extrude(context, id + "F34", {"entities" : qUnion([Q0]), "operationType" : NewBodyOperationType.REMOVE, "endBound" : BoundingType.UP_TO_NEXT, "oppositeDirection" : true, "depth" : 25.4 * mm, "offsetDistance" : 25.4 * mm});
        }
        {
            var Q0;
            {var subQ0=sQuery(id+"F11.wireOp",EDGE,"E40.1");var subQ1=makeQuery(id+"F12.opExtrude","SWEPT_FACE",FACE,{"disambiguationData":[OSD([subQ0])]});var subQ11=makeQuery(id+"F9.opExtrude","SWEPT_FACE",FACE,{"disambiguationData":[OSD([sQuery(id+"F8.wireOp",EDGE,"E23")])]});Q0=makeQuery(id+"FiTiTFmtsTyTFf0_2.1.F19.boolean.opBoolean","SPLIT",FACE,{"disambiguationData":[TD([subQ11])],"derivedFrom":makeQuery(id+"F19.boolean.opBoolean","SPLIT",FACE,{"disambiguationData":[TD([subQ11])],"derivedFrom":subQ1})});}
            var sketch = newSketch(context, id + "F35", { "sketchPlane" : qUnion([Q0])});
            skLineSegment(sketch, "E70.bottom", {"start": v(6, 43.69) * mm, "end": v(-6, 43.69) * mm});
            skLineSegment(sketch, "E70.top", {"start": v(6, 46.23) * mm, "end": v(-6, 46.23) * mm});
            skLineSegment(sketch, "E70.left", {"start": v(6, 43.69) * mm, "end": v(6, 46.23) * mm});
            skLineSegment(sketch, "E70.right", {"start": v(-6, 43.69) * mm, "end": v(-6, 46.23) * mm});
            skPoint(sketch, "E70.middle", {"position": v(0, 44.96) * mm});
            skSolve(sketch);
        }
        {
            var Q0;
            Q0 = qSketchRegion(id + "F35", true);
            extrude(context, id + "F36", {"entities" : qUnion([Q0]), "operationType" : NewBodyOperationType.REMOVE, "oppositeDirection" : true, "depth" : 1.27 * mm, "offsetDistance" : 25.4 * mm, "hasSecondDirection" : true, "secondDirectionOppositeDirection" : false, "secondDirectionDepth" : 8 * mm});
        }
        {
            var Q0;
            {var subQ2=sQuery(id+"F35.wireOp",EDGE,"E70.bottom");Q0=makeQuery(id+"F36.boolean.opBoolean","COPY",FACE,{"disambiguationData":[TD([makeQuery(id+"F28.opExtrude","SWEPT_FACE",FACE,{"disambiguationData":[OSD([sQuery(id+"F27.wireOp",EDGE,"E61")])]})])],"derivedFrom":makeQuery(id+"F36.opExtrude","SWEPT_FACE",FACE,{"disambiguationData":[OSD([subQ2])]})});}
            var sketch = newSketch(context, id + "F37", { "sketchPlane" : qUnion([Q0])});
            skLineSegment(sketch, "E71.bottom", {"start": v(-6, -15.78) * mm, "end": v(6, -15.78) * mm, "construction": true});
            skLineSegment(sketch, "E71.top", {"start": v(-6, -25.05) * mm, "end": v(6, -25.05) * mm, "construction": true});
            skLineSegment(sketch, "E71.left", {"start": v(-6, -15.78) * mm, "end": v(-6, -25.05) * mm, "construction": true});
            skLineSegment(sketch, "E71.right", {"start": v(6, -15.78) * mm, "end": v(6, -25.05) * mm, "construction": true});
            skLineSegment(sketch, "E72.0", {"start": v(-4.73, -23.78) * mm, "end": v(4.73, -23.78) * mm});
            skLineSegment(sketch, "E72.1", {"start": v(-4.73, -17.05) * mm, "end": v(-4.73, -23.78) * mm});
            skLineSegment(sketch, "E72.2", {"start": v(-4.73, -17.05) * mm, "end": v(4.73, -17.05) * mm});
            skLineSegment(sketch, "E72.3", {"start": v(4.73, -17.05) * mm, "end": v(4.73, -23.78) * mm});
            skSolve(sketch);
        }
        {
            var Q0;
            Q0 = qSketchRegion(id + "F37", true);
            extrude(context, id + "F38", {"entities" : qUnion([Q0]), "operationType" : NewBodyOperationType.REMOVE, "endBound" : BoundingType.UP_TO_NEXT, "oppositeDirection" : true, "depth" : 25.4 * mm, "offsetDistance" : 25.4 * mm});
        }
        {
            var Q0;
            Q0=makeQuery(id+"F28.opExtrude","SWEPT_FACE",FACE,{"disambiguationData":[OSD([sQuery(id+"F27.wireOp",EDGE,"E59.0")])]});
            var sketch = newSketch(context, id + "F39", { "sketchPlane" : qUnion([Q0])});
            skLineSegment(sketch, "E73", {"start": v(-30.48, -8.59) * mm, "end": v(30.48, -8.59) * mm});
            skLineSegment(sketch, "E74", {"start": v(-30.48, -8.59) * mm, "end": v(-30.48, 44.96) * mm});
            skLineSegment(sketch, "E75", {"start": v(30.48, -8.59) * mm, "end": v(30.48, 44.96) * mm});
            skLineSegment(sketch, "E76.0", {"start": v(-30.35, -8.46) * mm, "end": v(-30.35, 44.96) * mm});
            skLineSegment(sketch, "E76.1", {"start": v(-30.35, -8.46) * mm, "end": v(30.35, -8.46) * mm});
            skLineSegment(sketch, "E76.2", {"start": v(30.35, -8.46) * mm, "end": v(30.35, 44.96) * mm});
            skLineSegment(sketch, "E77", {"start": v(-30.48, 44.96) * mm, "end": v(-30.35, 44.96) * mm});
            skLineSegment(sketch, "E78", {"start": v(30.48, 44.96) * mm, "end": v(30.35, 44.96) * mm});
            skSolve(sketch);
        }
        {
            var Q0;
            Q0 = qSketchRegion(id + "F39", true);
            extrude(context, id + "F40", {"entities" : qUnion([Q0]), "operationType" : NewBodyOperationType.REMOVE, "endBound" : BoundingType.THROUGH_ALL, "oppositeDirection" : true, "depth" : 25.4 * mm, "offsetDistance" : 25.4 * mm});
        }
        {
            var Q0;
            Q0=qCreatedBy(makeId("Right.planeOp"),FACE);
            var sketch = newSketch(context, id + "F41", { "sketchPlane" : qUnion([Q0])});
            skLineSegment(sketch, "E79.0", {"start": v(-18, -6.35) * mm, "end": v(-18, -5.65) * mm, "construction": true});
            skLineSegment(sketch, "E80.0", {"start": v(-17.75, -5.5) * mm, "end": v(-17.75, -6.5) * mm, "construction": true});
            skLineSegment(sketch, "E81", {"start": v(-18, -6) * mm, "end": v(-13.35, -6) * mm, "construction": true});
            skLineSegment(sketch, "E82", {"start": v(-17.75, -5.5) * mm, "end": v(-14.14, -5.5) * mm});
            skLineSegment(sketch, "E83", {"start": v(-14.14, -5.5) * mm, "end": v(-14.14, -2.19) * mm});
            skLineSegment(sketch, "E84", {"start": v(-14.14, -2.19) * mm, "end": v(-19.59, -2.19) * mm});
            skLineSegment(sketch, "E85", {"start": v(-19.59, -2.19) * mm, "end": v(-19.59, -6) * mm});
            skLineSegment(sketch, "E86", {"start": v(-19.59, -6) * mm, "end": v(-18, -6) * mm});
            skLineSegment(sketch, "E87", {"start": v(-18, -6) * mm, "end": v(-18, -5.5) * mm});
            skLineSegment(sketch, "E88", {"start": v(-18, -5.5) * mm, "end": v(-17.75, -5.5) * mm});
            skSolve(sketch);
        }
        {
            var Q0;
            Q0 = qSketchRegion(id + "F41", true);
            var Q1;
            Q1=sQuery(id+"F41.wireOp",EDGE,"E86");
            revolve(context, id + "F42", {"surfaceOperationType" : NewSurfaceOperationType.NEW, "entities" : qUnion([Q0]), "axis" : qUnion([Q1]), "revolveType" : RevolveType.FULL});
        }
        {
            var Q0;
            Q0=makeQuery(id+"F42.opRevolve","SWEPT_FACE",FACE,{"disambiguationData":[OSD([sQuery(id+"F41.wireOp",EDGE,"E83")])]});
            var sketch = newSketch(context, id + "F43", { "sketchPlane" : qUnion([Q0])});
            skLineSegment(sketch, "E89.bottom", {"start": v(0.95, -2.31) * mm, "end": v(-0.95, -2.31) * mm});
            skLineSegment(sketch, "E89.top", {"start": v(0.95, 24.48) * mm, "end": v(-0.95, 24.48) * mm});
            skLineSegment(sketch, "E89.left", {"start": v(0.95, -2.31) * mm, "end": v(0.95, 24.48) * mm});
            skLineSegment(sketch, "E89.right", {"start": v(-0.95, -2.31) * mm, "end": v(-0.95, 24.48) * mm});
            skCircle(sketch, "E90.0", {"center": v(0, -6) * mm, "radius": 0.35 * mm, "construction": true});
            skSolve(sketch);
        }
        {
            var Q0;
            Q0 = qSketchRegion(id + "F43", true);
            extrude(context, id + "F44", {"entities" : qUnion([Q0]), "operationType" : NewBodyOperationType.ADD, "oppositeDirection" : true, "depth" : 3.17 * mm, "offsetDistance" : 25.4 * mm});
        }
        {
            var Q0;
            Q0=makeQuery(id+"F42.opRevolve","SWEPT_EDGE",EDGE,{"disambiguationData":[OSD([sQuery(id+"F41.wireOp",EDGE,"E84"),sQuery(id+"F41.wireOp",EDGE,"E85")])]});
            chamfer(context, id + "F45", {"entities" : qUnion([Q0]), "width" : 1.9 * mm, "tangentPropagation" : true});
        }
        {
            var Q0;
            Q0=makeQuery(id+"F44.opExtrude","SWEPT_FACE",FACE,{"disambiguationData":[OSD([sQuery(id+"F43.wireOp",EDGE,"E89.top")])]});
            var sketch = newSketch(context, id + "F46", { "sketchPlane" : qUnion([Q0])});
            skLineSegment(sketch, "E91", {"start": v(0.27, -17.32) * mm, "end": v(0.95, -14.78) * mm});
            skLineSegment(sketch, "E92", {"start": v(-0.27, -17.32) * mm, "end": v(-0.95, -14.78) * mm});
            skLineSegment(sketch, "E93", {"start": v(-0.95, -14.78) * mm, "end": v(-0.95, -17.32) * mm});
            skLineSegment(sketch, "E94", {"start": v(-0.95, -17.32) * mm, "end": v(-0.27, -17.32) * mm});
            skLineSegment(sketch, "E95", {"start": v(0.27, -17.32) * mm, "end": v(0.95, -17.32) * mm});
            skLineSegment(sketch, "E96", {"start": v(0.95, -17.32) * mm, "end": v(0.95, -14.78) * mm});
            skSolve(sketch);
        }
        {
            var Q0;
            Q0 = qSketchRegion(id + "F46", true);
            var Q1;
            Q1=makeQuery(id+"F42.opRevolve","SWEPT_FACE",FACE,{"disambiguationData":[OSD([sQuery(id+"F41.wireOp",EDGE,"E84")])]});
            extrude(context, id + "F47", {"entities" : qUnion([Q0]), "operationType" : NewBodyOperationType.REMOVE, "endBound" : BoundingType.UP_TO_SURFACE, "oppositeDirection" : true, "depth" : 25.4 * mm, "endBoundEntityFace" : qUnion([Q1]), "offsetDistance" : 25.4 * mm});
        }
        {
            var Q0;
            Q0=makeQuery(id+"F44.boolean.opBoolean","MERGE",FACE,{"derivedFrom":[makeQuery(id+"F42.opRevolve","SWEPT_FACE",FACE,{"disambiguationData":[OSD([sQuery(id+"F41.wireOp",EDGE,"E83")])]}),makeQuery(id+"F44.opExtrude","CAP_FACE",FACE,{"disambiguationData":[OSD([sQuery(id+"F43.wireOp",EDGE,"E89.bottom"),sQuery(id+"F43.wireOp",EDGE,"E89.top"),sQuery(id+"F43.wireOp",EDGE,"E89.left"),sQuery(id+"F43.wireOp",EDGE,"E89.right")])],"isStart":true})]});
            var sketch = newSketch(context, id + "F48", { "sketchPlane" : qUnion([Q0])});
            skCircle(sketch, "E97", {"center": v(0, -6) * mm, "radius": 0.5 * mm, "construction": true});
            skCircle(sketch, "E98.0", {"center": v(0, -6) * mm, "radius": 0.58 * mm});
            skSolve(sketch);
        }
        {
            var Q0;
            Q0=makeQuery(id+"F42.opRevolve","SWEPT_FACE",FACE,{"disambiguationData":[OSD([sQuery(id+"F41.wireOp",EDGE,"E87")])]});
            var sketch = newSketch(context, id + "F49", { "sketchPlane" : qUnion([Q0])});
            skCircle(sketch, "E99.0", {"center": v(0, -6) * mm, "radius": 0.5 * mm});
            skSolve(sketch);
        }
        {
            var Q0;
            Q0 = qSketchRegion(id + "F49", true);
            var Q1;
            Q1=makeQuery(id+"F44.boolean.opBoolean","MERGE",FACE,{"derivedFrom":[makeQuery(id+"F42.opRevolve","SWEPT_FACE",FACE,{"disambiguationData":[OSD([sQuery(id+"F41.wireOp",EDGE,"E83")])]}),makeQuery(id+"F44.opExtrude","CAP_FACE",FACE,{"disambiguationData":[OSD([sQuery(id+"F43.wireOp",EDGE,"E89.bottom"),sQuery(id+"F43.wireOp",EDGE,"E89.top"),sQuery(id+"F43.wireOp",EDGE,"E89.left"),sQuery(id+"F43.wireOp",EDGE,"E89.right")])],"isStart":true})]});
            extrude(context, id + "F50", {"entities" : qUnion([Q0]), "operationType" : NewBodyOperationType.ADD, "endBound" : BoundingType.UP_TO_SURFACE, "depth" : 25.4 * mm, "endBoundEntityFace" : qUnion([Q1]), "offsetDistance" : 25.4 * mm});
        }
        {
            var Q0;
            Q0=qCreatedBy(makeId("Right.planeOp"),FACE);
            var sketch = newSketch(context, id + "F51", { "sketchPlane" : qUnion([Q0])});
            skLineSegment(sketch, "E100", {"start": v(-19.59, -6) * mm, "end": v(-18.34, -6) * mm});
            skLineSegment(sketch, "E101", {"start": v(-18.34, -6) * mm, "end": v(-19.59, -4.75) * mm});
            skLineSegment(sketch, "E102", {"start": v(-19.59, -4.75) * mm, "end": v(-19.59, -6) * mm});
            skSolve(sketch);
        }
        {
            var Q0;
            Q0 = qSketchRegion(id + "F51", true);
            var Q1;
            Q1=sQuery(id+"F51.wireOp",EDGE,"E100");
            revolve(context, id + "F52", {"operationType" : NewBodyOperationType.REMOVE, "surfaceOperationType" : NewSurfaceOperationType.NEW, "entities" : qUnion([Q0]), "axis" : qUnion([Q1]), "revolveType" : RevolveType.FULL, "oppositeDirection" : true});
        }
        {
            var Q0;
            Q0=makeQuery(id+"F42.opRevolve","SWEPT_FACE",FACE,{"disambiguationData":[OSD([sQuery(id+"F41.wireOp",EDGE,"E85")])]});
            var sketch = newSketch(context, id + "F53", { "sketchPlane" : qUnion([Q0])});
            skLineSegment(sketch, "E103.bottom", {"start": v(-0.37, -4.1) * mm, "end": v(0.38, -4.1) * mm});
            skLineSegment(sketch, "E103.top", {"start": v(-0.37, -9.8) * mm, "end": v(0.38, -9.8) * mm});
            skLineSegment(sketch, "E103.left", {"start": v(-0.37, -4.1) * mm, "end": v(-0.37, -9.8) * mm});
            skLineSegment(sketch, "E103.right", {"start": v(0.38, -4.1) * mm, "end": v(0.38, -9.8) * mm});
            skPoint(sketch, "E103.middle", {"position": v(0, -6.95) * mm});
            skSolve(sketch);
        }
        {
            var Q0;
            Q0 = qSketchRegion(id + "F53", true);
            extrude(context, id + "F54", {"entities" : qUnion([Q0]), "operationType" : NewBodyOperationType.REMOVE, "endBound" : BoundingType.THROUGH_ALL, "oppositeDirection" : true, "depth" : 25.4 * mm, "offsetDistance" : 25.4 * mm});
        }
        {
            var Q0;
            Q0=makeQuery(id+"F12.boolean.opBoolean","MERGE",FACE,{"derivedFrom":[makeQuery(id+"F7.opExtrude","CAP_FACE",FACE,{"disambiguationData":[OSD([sQuery(id+"F6.wireOp",EDGE,"E14.bottom"),sQuery(id+"F6.wireOp",EDGE,"E14.top"),sQuery(id+"F6.wireOp",EDGE,"E14.left"),sQuery(id+"F6.wireOp",EDGE,"E14.right"),sQuery(id+"F6.wireOp",EDGE,"E15.0")])],"isStart":false}),makeQuery(id+"F12.opExtrude","CAP_FACE",FACE,{"disambiguationData":[OSD([sQuery(id+"F11.wireOp",EDGE,"E32"),sQuery(id+"F11.wireOp",EDGE,"E33"),sQuery(id+"F11.wireOp",EDGE,"E34"),sQuery(id+"F11.wireOp",EDGE,"E35"),sQuery(id+"F11.wireOp",EDGE,"E39"),sQuery(id+"F11.wireOp",EDGE,"E40.0"),sQuery(id+"F11.wireOp",EDGE,"E40.1"),sQuery(id+"F11.wireOp",EDGE,"E40.2"),sQuery(id+"F11.wireOp",EDGE,"E41"),sQuery(id+"F11.wireOp",EDGE,"E42")])],"isStart":true})]});
            var sketch = newSketch(context, id + "F55", { "sketchPlane" : qUnion([Q0])});
            skLineSegment(sketch, "E104.bottom", {"start": v(-29.84, 28.93) * mm, "end": v(29.84, 28.93) * mm});
            skLineSegment(sketch, "E104.top", {"start": v(-29.84, -28.23) * mm, "end": v(29.84, -28.23) * mm});
            skLineSegment(sketch, "E104.left", {"start": v(-29.84, 28.93) * mm, "end": v(-29.84, -28.23) * mm});
            skLineSegment(sketch, "E104.right", {"start": v(29.84, 28.93) * mm, "end": v(29.84, -28.23) * mm});
            skSolve(sketch);
        }
        {
            var Q0;
            Q0 = qSketchRegion(id + "F55", true);
            extrude(context, id + "F56", {"entities" : qUnion([Q0]), "depth" : 0.25 * mm, "offsetDistance" : 25.4 * mm});
        }
        {
            var Q0;
            Q0=makeQuery(id+"F56.opExtrude","CAP_FACE",FACE,{"disambiguationData":[OSD([sQuery(id+"F55.wireOp",EDGE,"E104.bottom"),sQuery(id+"F55.wireOp",EDGE,"E104.top"),sQuery(id+"F55.wireOp",EDGE,"E104.left"),sQuery(id+"F55.wireOp",EDGE,"E104.right")])],"isStart":false});
            var sketch = newSketch(context, id + "F57", { "sketchPlane" : qUnion([Q0])});
            skArc(sketch, "E105", {"start": v(15.49, -14.06) * mm, "mid": v(0, 11.46) * mm, "end": v(-15.49, -14.06) * mm});
            skArc(sketch, "E106.0", {"start": v(16.05, -14.36) * mm, "mid": v(0, 12.1) * mm, "end": v(-16.05, -14.36) * mm});
            skLineSegment(sketch, "E107", {"start": v(-15.49, -14.06) * mm, "end": v(-16.05, -14.36) * mm});
            skLineSegment(sketch, "E108", {"start": v(16.05, -14.36) * mm, "end": v(15.49, -14.06) * mm});
            skSolve(sketch);
        }
        {
            var Q0;
            Q0 = qSketchRegion(id + "F57", true);
            extrude(context, id + "F58", {"entities" : qUnion([Q0]), "operationType" : NewBodyOperationType.REMOVE, "oppositeDirection" : true, "depth" : 0.03 * mm, "offsetDistance" : 25.4 * mm});
        }
        {
            var Q0;
            Q0=makeQuery(id+"F56.opExtrude","CAP_FACE",FACE,{"disambiguationData":[OSD([sQuery(id+"F55.wireOp",EDGE,"E104.bottom"),sQuery(id+"F55.wireOp",EDGE,"E104.top"),sQuery(id+"F55.wireOp",EDGE,"E104.left"),sQuery(id+"F55.wireOp",EDGE,"E104.right")])],"isStart":false});
            var sketch = newSketch(context, id + "F59", { "sketchPlane" : qUnion([Q0])});
            skPoint(sketch, "E109.orphan", {"position": v(15.49, -14.06) * mm});
            skLineSegment(sketch, "E110", {"start": v(-15.64, -13.78) * mm, "end": v(-15.34, -14.34) * mm});
            skLineSegment(sketch, "E111", {"start": v(-15.34, -14.34) * mm, "end": v(-17.03, -15.22) * mm});
            skLineSegment(sketch, "E112", {"start": v(-17.03, -15.22) * mm, "end": v(-17.33, -14.66) * mm});
            skLineSegment(sketch, "E113", {"start": v(-17.33, -14.66) * mm, "end": v(-15.64, -13.78) * mm});
            skSolve(sketch);
        }
        {
            var Q0;
            Q0=makeQuery(id+"F56.opExtrude","CAP_FACE",FACE,{"disambiguationData":[OSD([sQuery(id+"F55.wireOp",EDGE,"E104.bottom"),sQuery(id+"F55.wireOp",EDGE,"E104.top"),sQuery(id+"F55.wireOp",EDGE,"E104.left"),sQuery(id+"F55.wireOp",EDGE,"E104.right")])],"isStart":false});
            var sketch = newSketch(context, id + "F60", { "sketchPlane" : qUnion([Q0])});
            skLineSegment(sketch, "E114", {"start": v(-15.49, -14.06) * mm, "end": v(-15.34, -14.34) * mm});
            skLineSegment(sketch, "E115", {"start": v(-15.34, -14.34) * mm, "end": v(-18.72, -16.1) * mm});
            skLineSegment(sketch, "E116", {"start": v(-18.72, -16.1) * mm, "end": v(-19.02, -15.54) * mm});
            skLineSegment(sketch, "E117", {"start": v(-19.02, -15.54) * mm, "end": v(-15.63, -13.78) * mm});
            skLineSegment(sketch, "E118", {"start": v(-15.63, -13.78) * mm, "end": v(-15.49, -14.06) * mm});
            skSolve(sketch);
        }
        {
            var Q0;
            Q0 = qSketchRegion(id + "F59", true);
            extrude(context, id + "F61", {"entities" : qUnion([Q0]), "operationType" : NewBodyOperationType.REMOVE, "oppositeDirection" : true, "depth" : 0.03 * mm, "offsetDistance" : 25.4 * mm});
        }
        {
            var Q0;
            Q0 = qSketchRegion(id + "F60", true);
            extrude(context, id + "F62", {"entities" : qUnion([Q0]), "operationType" : NewBodyOperationType.REMOVE, "oppositeDirection" : true, "depth" : 0.03 * mm, "offsetDistance" : 25.4 * mm});
        }
        {
            var Q0;
            Q0=makeQuery(id+"F56.opExtrude","CAP_FACE",FACE,{"disambiguationData":[OSD([sQuery(id+"F55.wireOp",EDGE,"E104.bottom"),sQuery(id+"F55.wireOp",EDGE,"E104.top"),sQuery(id+"F55.wireOp",EDGE,"E104.left"),sQuery(id+"F55.wireOp",EDGE,"E104.right")])],"isStart":false});
            var sketch = newSketch(context, id + "F63", { "sketchPlane" : qUnion([Q0])});
            skLineSegment(sketch, "E119", {"start": v(-22.1, -17.86) * mm, "end": v(-22.4, -17.3) * mm, "construction": true});
            skText(sketch, "E120", { "text": "0", "fontName": "OpenSans-Regular.ttf"});
            skPoint(sketch, "E121", {"position": v(-22.25, -17.58) * mm});
            skLineSegment(sketch, "E122", {"start": v(-22.25, -17.58) * mm, "end": v(-18.87, -15.82) * mm, "construction": true});
            skLineSegment(sketch, "E123", {"start": v(-21.22, -7.48) * mm, "end": v(-25.02, -7.75) * mm, "construction": true});
            skLineSegment(sketch, "E124", {"start": v(-20.05, 1.1) * mm, "end": v(-23.64, 2.37) * mm, "construction": true});
            skLineSegment(sketch, "E125", {"start": v(-15.56, 8.5) * mm, "end": v(-18.34, 11.1) * mm, "construction": true});
            skLineSegment(sketch, "E126", {"start": v(-8.48, 13.5) * mm, "end": v(-10, 17) * mm, "construction": true});
            skLineSegment(sketch, "E127", {"start": v(0, 15.27) * mm, "end": v(0, 19.08) * mm, "construction": true});
            skLineSegment(sketch, "E128", {"start": v(8.48, 13.5) * mm, "end": v(10, 17) * mm, "construction": true});
            skLineSegment(sketch, "E129", {"start": v(15.56, 8.5) * mm, "end": v(18.34, 11.1) * mm, "construction": true});
            skLineSegment(sketch, "E130", {"start": v(20.05, 1.1) * mm, "end": v(23.64, 2.37) * mm, "construction": true});
            skLineSegment(sketch, "E131", {"start": v(21.2, -7.48) * mm, "end": v(25, -7.75) * mm, "construction": true});
            skPoint(sketch, "E131.startSnap0", {"position": v(21.22, -7.48) * mm});
            skLineSegment(sketch, "E132", {"start": v(18.87, -15.82) * mm, "end": v(22.25, -17.58) * mm, "construction": true});
            skLineSegment(sketch, "E133", {"start": v(-23.75, 2.07) * mm, "end": v(-23.54, 2.67) * mm, "construction": true});
            skLineSegment(sketch, "E134", {"start": v(-25.04, -7.43) * mm, "end": v(-25, -8.07) * mm, "construction": true});
            skLineSegment(sketch, "E135", {"start": v(-18.56, 10.87) * mm, "end": v(-18.13, 11.34) * mm, "construction": true});
            skLineSegment(sketch, "E136", {"start": v(-10.3, 16.88) * mm, "end": v(-9.71, 17.13) * mm, "construction": true});
            skLineSegment(sketch, "E137", {"start": v(-0.32, 19.08) * mm, "end": v(0.32, 19.08) * mm, "construction": true});
            skLineSegment(sketch, "E138", {"start": v(9.71, 17.13) * mm, "end": v(10.3, 16.88) * mm, "construction": true});
            skLineSegment(sketch, "E139", {"start": v(18.13, 11.34) * mm, "end": v(18.56, 10.87) * mm, "construction": true});
            skLineSegment(sketch, "E140", {"start": v(23.54, 2.67) * mm, "end": v(23.75, 2.07) * mm, "construction": true});
            skLineSegment(sketch, "E141", {"start": v(25.02, -7.43) * mm, "end": v(24.98, -8.07) * mm, "construction": true});
            skLineSegment(sketch, "E142", {"start": v(22.4, -17.3) * mm, "end": v(22.1, -17.86) * mm, "construction": true});
            skText(sketch, "E143", { "text": "10", "fontName": "OpenSans-Regular.ttf"});
            skText(sketch, "E144", { "text": "20", "fontName": "OpenSans-Regular.ttf"});
            skText(sketch, "E145", { "text": "30", "fontName": "OpenSans-Regular.ttf"});
            skText(sketch, "E146", { "text": "40", "fontName": "OpenSans-Regular.ttf"});
            skText(sketch, "E147", { "text": "50", "fontName": "OpenSans-Regular.ttf"});
            skText(sketch, "E148", { "text": "60", "fontName": "OpenSans-Regular.ttf"});
            skText(sketch, "E149", { "text": "70", "fontName": "OpenSans-Regular.ttf"});
            skText(sketch, "E150", { "text": "80", "fontName": "OpenSans-Regular.ttf"});
            skText(sketch, "E151", { "text": "90", "fontName": "OpenSans-Regular.ttf"});
            skText(sketch, "E152", { "text": "100", "fontName": "OpenSans-Regular.ttf"});
            const initialGuessF63  = {"E120": [-0.0215, -0.01902, -0.46175, 0.88701, 0.00397], "E143": [-0.0248, -0.01094, -0.06976, 0.99756, 0.00397], "E144": [-0.0247, -0.00064, 0.3338, 0.94264, 0.00397], "E145": [-0.02052, 0.00877, 0.682, 0.73135, 0.00397], "E146": [-0.01293, 0.01573, 0.91706, 0.39875, 0.00397], "E147": [-0.0032, 0.01908, 1, 0, 0.00397], "E148": [0.00707, 0.01828, 0.91706, -0.39875, 0.00397], "E149": [0.01617, 0.01344, 0.682, -0.73135, 0.00397], "E150": [0.02258, 0.00538, 0.3338, -0.94264, 0.00397], "E151": [0.02522, -0.00456, -0.06976, -0.99756, 0.00397], "E152": [0.02445, -0.01335, -0.46175, -0.88701, 0.00397]};
            skSetInitialGuess(sketch, initialGuessF63);
            skSolve(sketch);
        }
        {
            var Q0;
            Q0=makeQuery(id+"F56.opExtrude","CAP_FACE",FACE,{"disambiguationData":[OSD([sQuery(id+"F55.wireOp",EDGE,"E104.bottom"),sQuery(id+"F55.wireOp",EDGE,"E104.top"),sQuery(id+"F55.wireOp",EDGE,"E104.left"),sQuery(id+"F55.wireOp",EDGE,"E104.right")])],"isStart":false});
            var sketch = newSketch(context, id + "F64", { "sketchPlane" : qUnion([Q0])});
            skArc(sketch, "E153", {"start": v(4.57, -6) * mm, "mid": v(0, -1.43) * mm, "end": v(-4.57, -6) * mm});
            skLineSegment(sketch, "E154", {"start": v(-4.57, -6) * mm, "end": v(-4.57, -28.23) * mm});
            skLineSegment(sketch, "E155", {"start": v(-4.57, -28.23) * mm, "end": v(4.57, -28.23) * mm});
            skLineSegment(sketch, "E156", {"start": v(4.57, -28.23) * mm, "end": v(4.57, -6) * mm});
            skSolve(sketch);
        }
        {
            var Q0;
            Q0 = qSketchRegion(id + "F64", true);
            extrude(context, id + "F65", {"entities" : qUnion([Q0]), "operationType" : NewBodyOperationType.REMOVE, "endBound" : BoundingType.THROUGH_ALL, "oppositeDirection" : true, "depth" : 25.4 * mm, "offsetDistance" : 25.4 * mm});
        }
        {
            var Q0;
            Q0 = qSketchRegion(id + "F63", true);
            extrude(context, id + "F66", {"entities" : qUnion([Q0]), "operationType" : NewBodyOperationType.REMOVE, "oppositeDirection" : true, "depth" : 0.03 * mm, "offsetDistance" : 25.4 * mm});
        }
    });
